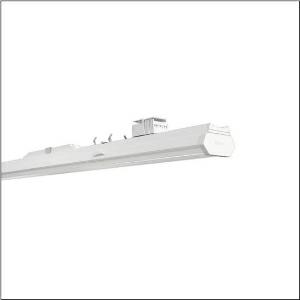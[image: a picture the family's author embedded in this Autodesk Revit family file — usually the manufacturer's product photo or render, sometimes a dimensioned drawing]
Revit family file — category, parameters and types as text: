
# Revit family: licross_r__11_protected_ho_51tp11cn4exs_0205
name_source: partatom
category: Lighting Fixtures
units: mm (PartAtom-declared; Revit-internal decimal feet)

## family parameters
Cut with Voids When Loaded = No
Host = Face
Light Source = No
Part Type = Normal
Room Calculation Point = No
Round Connector Dimension = Use Diameter
Shared = No

## types (1)
- --- (1 x LED, 14460 lm, 77.6 W, 4000K)
    Apparent Load = 78 VA
    CIE Flux Codes = 84 94 98 99 100
    Color Rendering = 80
    Color Temperature = 4000K
    Default Elevation = 1800 mm
    Description = Licross® 11 Protected HO, luminaire insert, of sheet steel, galvanised, coil coated, white, length: 1.500mm, width: 90mm, height: 101mm, LED rated luminous flux: 14.460lm, light colour: 840, control gear: ON/OFF Multilumen, CLOi, with plug, 3-pole, with phase selection, mains connection: 220..240V, AC, 50/60Hz, halogen-free wiring, primary light control with lens, of plastic, primary optical cover: cover, of PMMA, light emission: direct with ceiling illumination distribution, primary light characteristic: symmetric, protection rating (complete): IP64, insulation class (complete): insulation class I (protective earthing), certification: CE, ENEC, VDE, UKCA, protection symbol: D if used in an environment with conductive dust loads with corresponding accessories, impact resistance: IK06, permissible ambient temperature for indoor applications: -35..+35°C, corresponds to IFS (International Featured Standards) requirements for safety and quality in the food industry, reducing of maximum allowable ambient temperature of 5°C with ceiling mounting, LABS conformity tested according to VDMA 24364:2018-05, packaging unit: 1 piece
    Height = 92 mm
    Lamp = 1 x LED
    Lamp Light Flux = 14460 lm
    Lamp Power = 77.6 W
    Lamp count = 1
    Length = 1500 mm
    Luminous efficacy = 186 lm/W
    Manufacturer = Siteco
    ModVariant = No
    Model = 51TP11CN4EXS
    Mounting Place = Ceiling
    Mounting Type = Pendant
    Number of Poles = 1
    OnlyDefault = Yes
    Power Factor = 1
    Product Name = Licross® 11 Protected HO
    Product group = luminaire insert
    ProductGroupID = 902
    Protection Class = Protection class I
    Protection Degree = IP 64
    RLX_Detail_Level = 1
    RlxData = <blob elided: 22129 chars, md5=5a210ccc>
    Socket = socket
    Standby Power = 0 W
    System Light Flux = 14460 lm
    System Power = 78 W
    Type Comments = factory setting: luminous flux: 100 % | (A | C | E) | 181 mA
    Type Image = l_1256148.jpg
    URL = http://relux.com
    VarID = @adj_003755
    Voltage = 0 V
    Weight = 0.00 kg
    Width = 88 mm

## geometry (parser evidence)
native form markers: Blend x4, Sweep x12
no freeform markers — native parametric forms only
